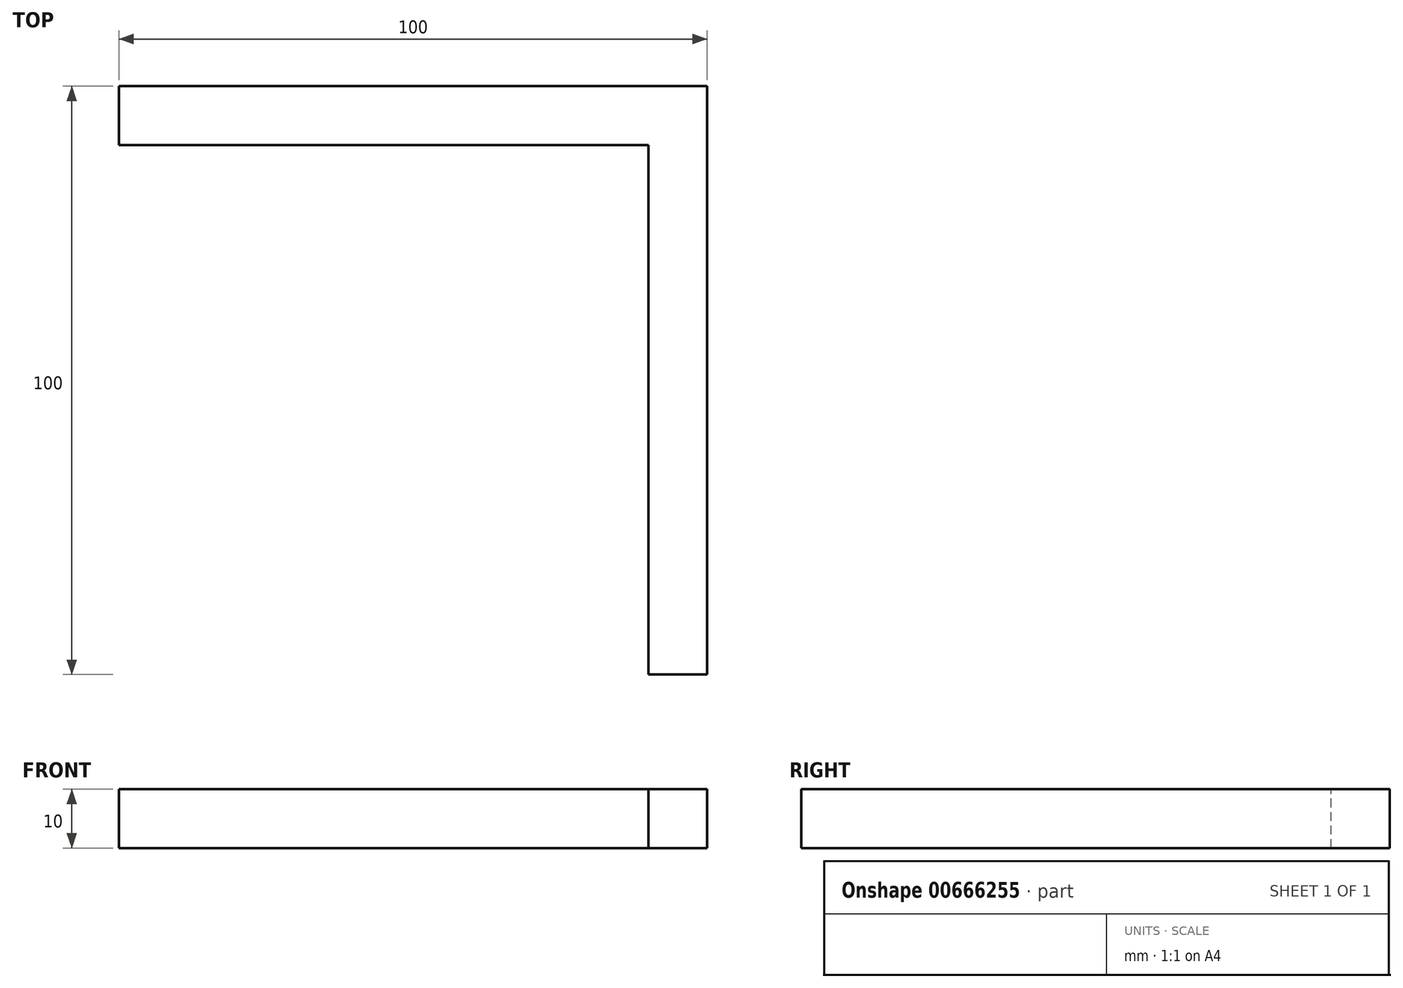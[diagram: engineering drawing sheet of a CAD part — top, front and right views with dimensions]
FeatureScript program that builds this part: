
annotation { "Feature Type Name" : "Feature", "Feature Type Description" : "" }
export const myFeature = defineFeature(function(context is Context, id is Id, definition is map)
    precondition{}
    {
        {
            var Q0;
            Q0=qCreatedBy(makeId("Top.planeOp"),FACE);
            var sketch = newSketch(context, id + "F0", { "sketchPlane" : qUnion([Q0])});
            skLineSegment(sketch, "E0.bottom", {"start": v(-50, 50) * mm, "end": v(50, 50) * mm});
            skLineSegment(sketch, "E0.top", {"start": v(-50, -50) * mm, "end": v(50, -50) * mm});
            skLineSegment(sketch, "E0.left", {"start": v(-50, 50) * mm, "end": v(-50, -50) * mm});
            skLineSegment(sketch, "E0.right", {"start": v(50, 50) * mm, "end": v(50, -50) * mm});
            skLineSegment(sketch, "E1", {"start": v(0, 0) * mm, "end": v(0, 50) * mm, "construction": true});
            skLineSegment(sketch, "E2", {"start": v(0, 0) * mm, "end": v(0, -50) * mm, "construction": true});
            skLineSegment(sketch, "E3", {"start": v(0, 0) * mm, "end": v(-50, 0) * mm, "construction": true});
            skSolve(sketch);
        }
        {
            var Q0;
            Q0 = qSketchRegion(id + "F0", true);
            extrude(context, id + "F1", {"entities" : qUnion([Q0]), "depth" : 10 * mm, "offsetDistance" : 25 * mm});
        }
        {
            var Q0;
            Q0=makeQuery(id+"F1.opExtrude","CAP_FACE",FACE,{"disambiguationData":[OSD([sQuery(id+"F0.wireOp",EDGE,"E0.bottom"),sQuery(id+"F0.wireOp",EDGE,"E0.top"),sQuery(id+"F0.wireOp",EDGE,"E0.left"),sQuery(id+"F0.wireOp",EDGE,"E0.right")])],"isStart":false});
            var sketch = newSketch(context, id + "F2", { "sketchPlane" : qUnion([Q0])});
            skLineSegment(sketch, "E4.bottom", {"start": v(-50, 40) * mm, "end": v(40, 40) * mm});
            skLineSegment(sketch, "E4.top", {"start": v(-50, -50) * mm, "end": v(40, -50) * mm});
            skLineSegment(sketch, "E4.left", {"start": v(-50, 40) * mm, "end": v(-50, -50) * mm});
            skLineSegment(sketch, "E4.right", {"start": v(40, 40) * mm, "end": v(40, -50) * mm});
            skSolve(sketch);
        }
        {
            var Q0;
            Q0 = qSketchRegion(id + "F2", true);
            extrude(context, id + "F3", {"entities" : qUnion([Q0]), "operationType" : NewBodyOperationType.REMOVE, "oppositeDirection" : true, "depth" : 25 * mm, "offsetDistance" : 25 * mm});
        }
    });
